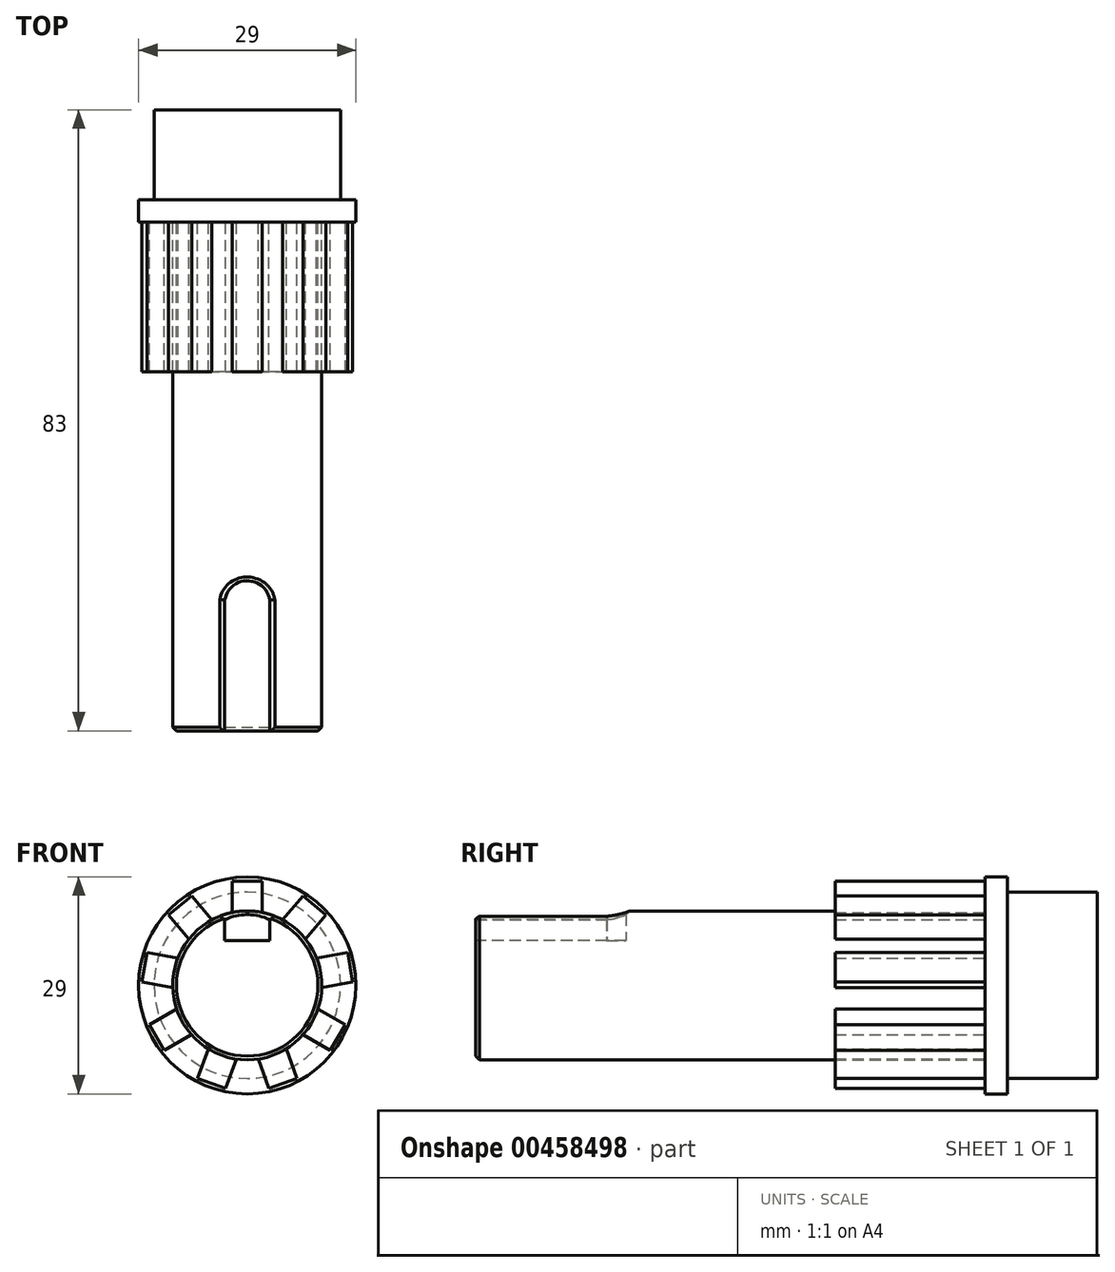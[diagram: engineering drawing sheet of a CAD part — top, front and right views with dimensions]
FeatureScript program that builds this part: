
annotation { "Feature Type Name" : "Feature", "Feature Type Description" : "" }
export const myFeature = defineFeature(function(context is Context, id is Id, definition is map)
    precondition{}
    {
        {
            var Q0;
            Q0=qCreatedBy(makeId("Front.planeOp"),FACE);
            var sketch = newSketch(context, id + "F0", { "sketchPlane" : qUnion([Q0])});
            skCircle(sketch, "E0", {"center": v(0, 0) * mm, "radius": 12.45 * mm});
            skSolve(sketch);
        }
        {
            var Q0;
            Q0=makeQuery(id+"F0.imprint","IMPRINT",FACE,{"disambiguationData":[TD([[makeQuery(id+"F0.imprint","IMPRINT",EDGE,{"derivedFrom":sQuery(id+"F0.wireOp",EDGE,"E0")}),1.0]])]});
            extrude(context, id + "F1", {"entities" : qUnion([Q0]), "oppositeDirection" : true, "depth" : 12 * mm});
        }
        {
            var Q0;
            Q0=qCreatedBy(makeId("Front.planeOp"),FACE);
            var sketch = newSketch(context, id + "F2", { "sketchPlane" : qUnion([Q0])});
            skCircle(sketch, "E1", {"center": v(0, 0) * mm, "radius": 14.5 * mm});
            skSolve(sketch);
        }
        {
            var Q0;
            Q0=makeQuery(id+"F2.imprint","IMPRINT",FACE,{"disambiguationData":[TD([[makeQuery(id+"F2.imprint","IMPRINT",EDGE,{"derivedFrom":sQuery(id+"F2.wireOp",EDGE,"E1")}),1.0]])]});
            extrude(context, id + "F3", {"entities" : qUnion([Q0]), "operationType" : NewBodyOperationType.ADD, "depth" : 3 * mm});
        }
        {
            var Q0;
            Q0=qCreatedBy(makeId("Front.planeOp"),FACE);
            cPlane(context, id + "F4", {"entities" : qUnion([Q0]), "cplaneType" : CPlaneType.OFFSET, "offset" : 3 * mm, "width" : 150 * mm, "height" : 150 * mm});
        }
        {
            var Q0;
            Q0=qCreatedBy(id+"F4.planeOp",FACE);
            var sketch = newSketch(context, id + "F5", { "sketchPlane" : qUnion([Q0])});
            skPoint(sketch, "E2.left.start.orphan", {"position": v(0, 9.95) * mm});
            skArc(sketch, "E3", {"start": v(-2, 9.75) * mm, "mid": v(0, -9.95) * mm, "end": v(2, 9.75) * mm});
            skLineSegment(sketch, "E4.top", {"start": v(0, 13.95) * mm, "end": v(2, 13.95) * mm});
            skLineSegment(sketch, "E4.right", {"start": v(2, 9.95) * mm, "end": v(2, 13.95) * mm});
            skLineSegment(sketch, "E5.top", {"start": v(0, 13.95) * mm, "end": v(-2, 13.95) * mm});
            skLineSegment(sketch, "E5.right", {"start": v(-2, 9.95) * mm, "end": v(-2, 13.95) * mm});
            skLineSegment(sketch, "E6", {"start": v(2, 13.95) * mm, "end": v(2, 9.95) * mm});
            skLineSegment(sketch, "E7", {"start": v(-2, 9.95) * mm, "end": v(-2, 9.75) * mm});
            skLineSegment(sketch, "E8", {"start": v(2, 9.95) * mm, "end": v(2, 9.75) * mm});
            skLineSegment(sketch, "E9", {"start": v(2, 9.75) * mm, "end": v(-2, 9.75) * mm});
            skLineSegment(sketch, "E10.1.0", {"start": v(-7.93, 6.34) * mm, "end": v(-10.5, 9.4) * mm});
            skLineSegment(sketch, "E10.1.1", {"start": v(-7.43, 11.97) * mm, "end": v(-4.86, 8.9) * mm});
            skLineSegment(sketch, "E10.1.2", {"start": v(-4.73, 8.75) * mm, "end": v(-7.8, 6.18) * mm});
            skLineSegment(sketch, "E10.1.3", {"start": v(-7.93, 6.34) * mm, "end": v(-7.8, 6.18) * mm});
            skLineSegment(sketch, "E10.1.4", {"start": v(-4.86, 8.9) * mm, "end": v(-4.73, 8.75) * mm});
            skLineSegment(sketch, "E10.1.5", {"start": v(-8.97, 10.69) * mm, "end": v(-7.43, 11.97) * mm});
            skLineSegment(sketch, "E10.1.6", {"start": v(-8.97, 10.69) * mm, "end": v(-10.5, 9.4) * mm});
            skLineSegment(sketch, "E10.2.0", {"start": v(-10.15, -0.24) * mm, "end": v(-14.09, 0.45) * mm});
            skLineSegment(sketch, "E10.2.1", {"start": v(-13.4, 4.4) * mm, "end": v(-9.45, 3.7) * mm});
            skLineSegment(sketch, "E10.2.2", {"start": v(-9.25, 3.66) * mm, "end": v(-9.95, -0.28) * mm});
            skLineSegment(sketch, "E10.2.3", {"start": v(-10.15, -0.24) * mm, "end": v(-9.95, -0.28) * mm});
            skLineSegment(sketch, "E10.2.4", {"start": v(-9.45, 3.7) * mm, "end": v(-9.25, 3.66) * mm});
            skLineSegment(sketch, "E10.2.5", {"start": v(-13.74, 2.42) * mm, "end": v(-13.4, 4.4) * mm});
            skLineSegment(sketch, "E10.2.6", {"start": v(-13.74, 2.42) * mm, "end": v(-14.09, 0.45) * mm});
            skLineSegment(sketch, "E10.3.0", {"start": v(-7.62, -6.7) * mm, "end": v(-11.08, -8.7) * mm});
            skLineSegment(sketch, "E10.3.1", {"start": v(-13.08, -5.24) * mm, "end": v(-9.62, -3.24) * mm});
            skLineSegment(sketch, "E10.3.2", {"start": v(-9.44, -3.14) * mm, "end": v(-7.44, -6.6) * mm});
            skLineSegment(sketch, "E10.3.3", {"start": v(-7.62, -6.7) * mm, "end": v(-7.44, -6.6) * mm});
            skLineSegment(sketch, "E10.3.4", {"start": v(-9.62, -3.24) * mm, "end": v(-9.44, -3.14) * mm});
            skLineSegment(sketch, "E10.3.5", {"start": v(-12.08, -6.97) * mm, "end": v(-13.08, -5.24) * mm});
            skLineSegment(sketch, "E10.3.6", {"start": v(-12.08, -6.97) * mm, "end": v(-11.08, -8.7) * mm});
            skLineSegment(sketch, "E10.4.0", {"start": v(-1.52, -10.03) * mm, "end": v(-2.9, -13.8) * mm});
            skLineSegment(sketch, "E10.4.1", {"start": v(-6.65, -12.42) * mm, "end": v(-5.28, -8.67) * mm});
            skLineSegment(sketch, "E10.4.2", {"start": v(-5.21, -8.48) * mm, "end": v(-1.45, -9.84) * mm});
            skLineSegment(sketch, "E10.4.3", {"start": v(-1.52, -10.03) * mm, "end": v(-1.45, -9.84) * mm});
            skLineSegment(sketch, "E10.4.4", {"start": v(-5.28, -8.67) * mm, "end": v(-5.21, -8.48) * mm});
            skLineSegment(sketch, "E10.4.5", {"start": v(-4.77, -13.1) * mm, "end": v(-6.65, -12.42) * mm});
            skLineSegment(sketch, "E10.4.6", {"start": v(-4.77, -13.1) * mm, "end": v(-2.9, -13.8) * mm});
            skLineSegment(sketch, "E10.5.0", {"start": v(5.28, -8.67) * mm, "end": v(6.65, -12.42) * mm});
            skLineSegment(sketch, "E10.5.1", {"start": v(2.9, -13.8) * mm, "end": v(1.52, -10.03) * mm});
            skLineSegment(sketch, "E10.5.2", {"start": v(1.45, -9.84) * mm, "end": v(5.21, -8.48) * mm});
            skLineSegment(sketch, "E10.5.3", {"start": v(5.28, -8.67) * mm, "end": v(5.21, -8.48) * mm});
            skLineSegment(sketch, "E10.5.4", {"start": v(1.52, -10.03) * mm, "end": v(1.45, -9.84) * mm});
            skLineSegment(sketch, "E10.5.5", {"start": v(4.77, -13.1) * mm, "end": v(2.9, -13.8) * mm});
            skLineSegment(sketch, "E10.5.6", {"start": v(4.77, -13.1) * mm, "end": v(6.65, -12.42) * mm});
            skLineSegment(sketch, "E10.6.0", {"start": v(9.62, -3.24) * mm, "end": v(13.08, -5.24) * mm});
            skLineSegment(sketch, "E10.6.1", {"start": v(11.08, -8.7) * mm, "end": v(7.62, -6.7) * mm});
            skLineSegment(sketch, "E10.6.2", {"start": v(7.44, -6.6) * mm, "end": v(9.44, -3.14) * mm});
            skLineSegment(sketch, "E10.6.3", {"start": v(9.62, -3.24) * mm, "end": v(9.44, -3.14) * mm});
            skLineSegment(sketch, "E10.6.4", {"start": v(7.62, -6.7) * mm, "end": v(7.44, -6.6) * mm});
            skLineSegment(sketch, "E10.6.5", {"start": v(12.08, -6.98) * mm, "end": v(11.08, -8.7) * mm});
            skLineSegment(sketch, "E10.6.6", {"start": v(12.08, -6.98) * mm, "end": v(13.08, -5.24) * mm});
            skLineSegment(sketch, "E10.7.0", {"start": v(9.45, 3.7) * mm, "end": v(13.4, 4.4) * mm});
            skLineSegment(sketch, "E10.7.1", {"start": v(14.09, 0.45) * mm, "end": v(10.15, -0.24) * mm});
            skLineSegment(sketch, "E10.7.2", {"start": v(9.95, -0.28) * mm, "end": v(9.25, 3.66) * mm});
            skLineSegment(sketch, "E10.7.3", {"start": v(9.45, 3.7) * mm, "end": v(9.25, 3.66) * mm});
            skLineSegment(sketch, "E10.7.4", {"start": v(10.15, -0.24) * mm, "end": v(9.95, -0.28) * mm});
            skLineSegment(sketch, "E10.7.5", {"start": v(13.74, 2.42) * mm, "end": v(14.09, 0.45) * mm});
            skLineSegment(sketch, "E10.7.6", {"start": v(13.74, 2.42) * mm, "end": v(13.4, 4.4) * mm});
            skLineSegment(sketch, "E10.8.0", {"start": v(4.86, 8.9) * mm, "end": v(7.43, 11.97) * mm});
            skLineSegment(sketch, "E10.8.1", {"start": v(10.5, 9.4) * mm, "end": v(7.93, 6.34) * mm});
            skLineSegment(sketch, "E10.8.2", {"start": v(7.8, 6.18) * mm, "end": v(4.73, 8.75) * mm});
            skLineSegment(sketch, "E10.8.3", {"start": v(4.86, 8.9) * mm, "end": v(4.73, 8.75) * mm});
            skLineSegment(sketch, "E10.8.4", {"start": v(7.93, 6.34) * mm, "end": v(7.8, 6.18) * mm});
            skLineSegment(sketch, "E10.8.5", {"start": v(8.97, 10.69) * mm, "end": v(10.5, 9.4) * mm});
            skLineSegment(sketch, "E10.8.6", {"start": v(8.97, 10.69) * mm, "end": v(7.43, 11.97) * mm});
            skSolve(sketch);
        }
        {
            var Q0;
            Q0=makeQuery(id+"F5.imprint","IMPRINT",FACE,{"disambiguationData":[TD([[makeQuery(id+"F5.imprint","IMPRINT",EDGE,{"derivedFrom":sQuery(id+"F5.wireOp",EDGE,"E4.left")}),1.0]])]});
            var Q1;
            Q1=makeQuery(id+"F5.imprint","IMPRINT",FACE,{"disambiguationData":[TD([[makeQuery(id+"F5.imprint","IMPRINT",EDGE,{"derivedFrom":sQuery(id+"F5.wireOp",EDGE,"E4.bottom")}),1.0]])]});
            var Q2;
            Q2=makeQuery(id+"F5.imprint","IMPRINT",FACE,{"disambiguationData":[TD([[makeQuery(id+"F5.imprint","IMPRINT",EDGE,{"derivedFrom":sQuery(id+"F5.wireOp",EDGE,"E4.top")}),-1.0]])]});
            var Q3;
            Q3=makeQuery(id+"F5.imprint","IMPRINT",FACE,{"disambiguationData":[TD([[makeQuery(id+"F5.imprint","IMPRINT",EDGE,{"derivedFrom":sQuery(id+"F5.wireOp",EDGE,"E10.1.0")}),-1.0]])]});
            var Q4;
            Q4=makeQuery(id+"F5.imprint","IMPRINT",FACE,{"disambiguationData":[TD([[makeQuery(id+"F5.imprint","IMPRINT",EDGE,{"derivedFrom":sQuery(id+"F5.wireOp",EDGE,"E10.2.0")}),-1.0]])]});
            var Q5;
            Q5=makeQuery(id+"F5.imprint","IMPRINT",FACE,{"disambiguationData":[TD([[makeQuery(id+"F5.imprint","IMPRINT",EDGE,{"derivedFrom":sQuery(id+"F5.wireOp",EDGE,"E10.3.0")}),-1.0]])]});
            var Q6;
            Q6=makeQuery(id+"F5.imprint","IMPRINT",FACE,{"disambiguationData":[TD([[makeQuery(id+"F5.imprint","IMPRINT",EDGE,{"derivedFrom":sQuery(id+"F5.wireOp",EDGE,"E10.4.0")}),-1.0]])]});
            var Q7;
            Q7=makeQuery(id+"F5.imprint","IMPRINT",FACE,{"disambiguationData":[TD([[makeQuery(id+"F5.imprint","IMPRINT",EDGE,{"derivedFrom":sQuery(id+"F5.wireOp",EDGE,"E10.5.0")}),-1.0]])]});
            var Q8;
            Q8=makeQuery(id+"F5.imprint","IMPRINT",FACE,{"disambiguationData":[TD([[makeQuery(id+"F5.imprint","IMPRINT",EDGE,{"derivedFrom":sQuery(id+"F5.wireOp",EDGE,"E10.6.0")}),-1.0]])]});
            var Q9;
            Q9=makeQuery(id+"F5.imprint","IMPRINT",FACE,{"disambiguationData":[TD([[makeQuery(id+"F5.imprint","IMPRINT",EDGE,{"derivedFrom":sQuery(id+"F5.wireOp",EDGE,"E10.7.0")}),-1.0]])]});
            var Q10;
            Q10=makeQuery(id+"F5.imprint","IMPRINT",FACE,{"disambiguationData":[TD([[makeQuery(id+"F5.imprint","IMPRINT",EDGE,{"derivedFrom":sQuery(id+"F5.wireOp",EDGE,"E10.8.0")}),-1.0]])]});
            extrude(context, id + "F6", {"entities" : qUnion([Q0, Q1, Q2, Q3, Q4, Q5, Q6, Q7, Q8, Q9, Q10]), "operationType" : NewBodyOperationType.ADD, "depth" : 20 * mm});
        }
        {
            var Q0;
            Q0=qCreatedBy(id+"F4.planeOp",FACE);
            var sketch = newSketch(context, id + "F7", { "sketchPlane" : qUnion([Q0])});
            skCircle(sketch, "E11", {"center": v(0, 0) * mm, "radius": 9.95 * mm});
            skSolve(sketch);
        }
        {
            var Q0;
            Q0=makeQuery(id+"F7.imprint","IMPRINT",FACE,{"disambiguationData":[TD([[makeQuery(id+"F7.imprint","IMPRINT",EDGE,{"derivedFrom":sQuery(id+"F7.wireOp",EDGE,"E11")}),1.0]])]});
            extrude(context, id + "F8", {"entities" : qUnion([Q0]), "operationType" : NewBodyOperationType.ADD, "depth" : 68 * mm});
        }
        {
            var Q0;
            Q0=qCreatedBy(makeId("Top.planeOp"),FACE);
            cPlane(context, id + "F9", {"entities" : qUnion([Q0]), "cplaneType" : CPlaneType.OFFSET, "offset" : 6 * mm, "width" : 150 * mm, "height" : 150 * mm});
        }
        {
            var Q0;
            Q0=qCreatedBy(id+"F9.planeOp",FACE);
            var sketch = newSketch(context, id + "F10", { "sketchPlane" : qUnion([Q0])});
            skPoint(sketch, "E12.bottom.start.orphan", {"position": v(0, -53.13) * mm});
            skPoint(sketch, "E13.MirrorCS.end.orphan", {"position": v(0, -50.94) * mm});
            skPoint(sketch, "E13.MirrorCS.start.orphan", {"position": v(-2.16, -56.9) * mm});
            skPoint(sketch, "E14.end.orphan", {"position": v(0, -56.9) * mm});
            skPoint(sketch, "E15.orphan", {"position": v(2.16, -56.9) * mm});
            skPoint(sketch, "E16.MirrorCS.end.orphan", {"position": v(0, -72.97) * mm});
            skPoint(sketch, "E16.MirrorCS.start.orphan", {"position": v(0, -72.5) * mm});
            skPoint(sketch, "E17", {"position": v(0, -71.98) * mm});
            skLineSegment(sketch, "E18", {"start": v(0, -71.98) * mm, "end": v(0, -71.94) * mm});
            skLineSegment(sketch, "E19.bottom", {"start": v(0, -50.94) * mm, "end": v(0.22, -50.94) * mm});
            skLineSegment(sketch, "E19.top", {"start": v(0, -71.94) * mm, "end": v(3, -71.94) * mm});
            skLineSegment(sketch, "E19.left", {"start": v(0, -50.94) * mm, "end": v(0, -50.98) * mm});
            skLineSegment(sketch, "E19.right", {"start": v(3, -53.51) * mm, "end": v(3, -71.94) * mm});
            skLineSegment(sketch, "E20.MirrorCS", {"start": v(-3, -53.47) * mm, "end": v(-3, -71.94) * mm});
            skLineSegment(sketch, "E21.MirrorCS", {"start": v(0, -50.94) * mm, "end": v(-0.23, -50.94) * mm});
            skLineSegment(sketch, "E22.MirrorCS", {"start": v(0, -71.94) * mm, "end": v(-3, -71.94) * mm});
            skArc(sketch, "E23", {"start": v(3, -53.51) * mm, "mid": v(0.02, -50.93) * mm, "end": v(-3, -53.47) * mm});
            skPoint(sketch, "E24.orphan", {"position": v(-3, -50.94) * mm});
            skPoint(sketch, "E25.orphan", {"position": v(3, -50.94) * mm});
            skSolve(sketch);
        }
        {
            var Q0;
            Q0=makeQuery(id+"F8.opExtrude","CAP_EDGE",EDGE,{"disambiguationData":[OSD([sQuery(id+"F7.wireOp",EDGE,"E11")])],"isStart":false});
            chamfer(context, id + "F11", {"entities" : qUnion([Q0]), "width" : 0.5 * mm, "tangentPropagation" : true});
        }
        {
            var Q0;
            Q0 = qSketchRegion(id + "F10", true);
            extrude(context, id + "F12", {"entities" : qUnion([Q0]), "operationType" : NewBodyOperationType.REMOVE, "depth" : 25 * mm});
        }
        {
            var Q0;
            Q0=makeQuery(id+"F12.boolean.opBoolean","INTERSECT",EDGE,{"derivedFrom":[makeQuery(id+"F8.opExtrude","SWEPT_FACE",FACE,{"disambiguationData":[OSD([sQuery(id+"F7.wireOp",EDGE,"E11")])]}),makeQuery(id+"F12.opExtrude","SWEPT_FACE",FACE,{"disambiguationData":[OSD([sQuery(id+"F10.wireOp",EDGE,"E20.MirrorCS")])]})]});
            var Q1;
            Q1=makeQuery(id+"F12.boolean.opBoolean","INTERSECT",EDGE,{"derivedFrom":[makeQuery(id+"F8.opExtrude","SWEPT_FACE",FACE,{"disambiguationData":[OSD([sQuery(id+"F7.wireOp",EDGE,"E11")])]}),makeQuery(id+"F12.opExtrude","SWEPT_FACE",FACE,{"disambiguationData":[OSD([sQuery(id+"F10.wireOp",EDGE,"E23")])]})]});
            var Q2;
            Q2=makeQuery(id+"F12.boolean.opBoolean","INTERSECT",EDGE,{"derivedFrom":[makeQuery(id+"F8.opExtrude","SWEPT_FACE",FACE,{"disambiguationData":[OSD([sQuery(id+"F7.wireOp",EDGE,"E11")])]}),makeQuery(id+"F12.opExtrude","SWEPT_FACE",FACE,{"disambiguationData":[OSD([sQuery(id+"F10.wireOp",EDGE,"E19.right")])]})]});
            chamfer(context, id + "F13", {"entities" : qUnion([Q0, Q1, Q2]), "width" : 0.5 * mm, "tangentPropagation" : true});
        }
    });
